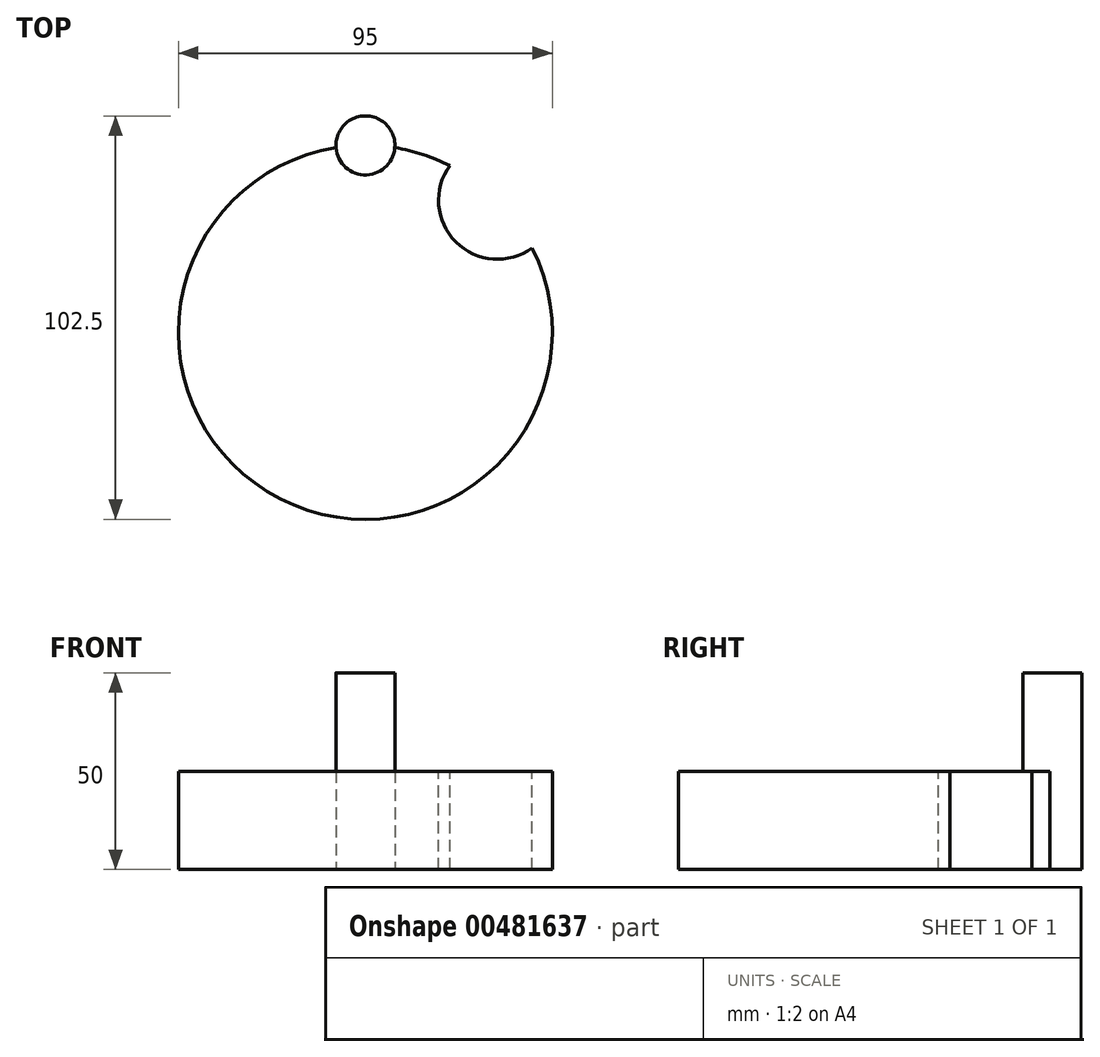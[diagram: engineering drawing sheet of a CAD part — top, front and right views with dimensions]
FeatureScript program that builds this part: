
annotation { "Feature Type Name" : "Feature", "Feature Type Description" : "" }
export const myFeature = defineFeature(function(context is Context, id is Id, definition is map)
    precondition{}
    {
        {
            var Q0;
            Q0=qCreatedBy(makeId("Top.planeOp"),FACE);
            var sketch = newSketch(context, id + "F0", { "sketchPlane" : qUnion([Q0])});
            skCircle(sketch, "E0", {"center": v(0, 0) * mm, "radius": 47.5 * mm});
            skCircle(sketch, "E1", {"center": v(0, 47.5) * mm, "radius": 7.5 * mm});
            skSolve(sketch);
        }
        {
            var Q0;
            {var subQ0=sQuery(id+"F0.wireOp",EDGE,"E1");var subQ1=sQuery(id+"F0.wireOp",EDGE,"E0");var subQ2=makeQuery(id+"F0.imprint","INTERSECT",VERTEX,{"disambiguationData":[OD(0.0)],"derivedFrom":[subQ1,subQ0]});Q0=makeQuery(id+"F0.imprint","IMPRINT",FACE,{"disambiguationData":[TD([[makeQuery(id+"F0.imprint","IMPRINT",EDGE,{"disambiguationData":[TD([[subQ2,-1.0]])],"derivedFrom":subQ1}),1.0]])]});}
            extrude(context, id + "F1", {"entities" : qUnion([Q0]), "depth" : 25 * mm, "offsetDistance" : 25 * mm});
        }
        {
            var Q0;
            {var subQ0=sQuery(id+"F0.wireOp",EDGE,"E1");var subQ1=sQuery(id+"F0.wireOp",EDGE,"E0");var subQ2=makeQuery(id+"F0.imprint","INTERSECT",VERTEX,{"disambiguationData":[OD(0.0)],"derivedFrom":[subQ1,subQ0]});Q0=makeQuery(id+"F0.imprint","IMPRINT",FACE,{"disambiguationData":[TD([[makeQuery(id+"F0.imprint","IMPRINT",EDGE,{"disambiguationData":[TD([[subQ2,1.0]])],"derivedFrom":subQ1}),1.0]])]});}
            var Q1;
            {var subQ0=sQuery(id+"F0.wireOp",EDGE,"E1");var subQ1=sQuery(id+"F0.wireOp",EDGE,"E0");var subQ2=makeQuery(id+"F0.imprint","INTERSECT",VERTEX,{"disambiguationData":[OD(0.0)],"derivedFrom":[subQ1,subQ0]});Q1=makeQuery(id+"F0.imprint","IMPRINT",FACE,{"disambiguationData":[TD([[makeQuery(id+"F0.imprint","IMPRINT",EDGE,{"disambiguationData":[TD([[subQ2,1.0]])],"derivedFrom":subQ1}),-1.0]])]});}
            extrude(context, id + "F2", {"entities" : qUnion([Q0, Q1]), "operationType" : NewBodyOperationType.ADD, "depth" : 50 * mm, "offsetDistance" : 25 * mm});
        }
        {
            var Q0;
            Q0=makeQuery(id+"F1.opExtrude","CAP_FACE",FACE,{"disambiguationData":[OSD([sQuery(id+"F0.wireOp",EDGE,"E0"),sQuery(id+"F0.wireOp",EDGE,"E1")])],"isStart":false});
            var sketch = newSketch(context, id + "F3", { "sketchPlane" : qUnion([Q0])});
            skCircle(sketch, "E2", {"center": v(33.59, 33.59) * mm, "radius": 15 * mm});
            skSolve(sketch);
        }
        {
            var Q0;
            {var subQ0=sQuery(id+"F3.wireOp",EDGE,"E2");var subQ1=sQuery(id+"F0.wireOp",EDGE,"E0");var subQ3=sQuery(id+"F0.wireOp",EDGE,"E1");var subQ5=makeQuery(id+"F2.opExtrude","SWEPT_FACE",FACE,{"disambiguationData":[OSD([subQ3])]});var subQ6=makeQuery(id+"FTU9S2BqntfehKC_1.3.F2.boolean.opBoolean","SPLIT",EDGE,{"disambiguationData":[TD([subQ5])],"derivedFrom":makeQuery(id+"FTU9S2BqntfehKC_1.2.F2.boolean.opBoolean","SPLIT",EDGE,{"disambiguationData":[TD([subQ5])],"derivedFrom":makeQuery(id+"FTU9S2BqntfehKC_1.1.F2.boolean.opBoolean","SPLIT",EDGE,{"disambiguationData":[OD(1.0)],"derivedFrom":makeQuery(id+"F1.opExtrude","CAP_EDGE",EDGE,{"disambiguationData":[OSD([subQ1])],"isStart":false})})})});var subQ7=makeQuery(id+"F3.imprint","INTERSECT",VERTEX,{"disambiguationData":[OD(0.0)],"derivedFrom":[subQ6,subQ0]});Q0=makeQuery(id+"F3.imprint","IMPRINT",FACE,{"disambiguationData":[TD([[makeQuery(id+"F3.imprint","IMPRINT",EDGE,{"disambiguationData":[TD([[subQ7,1.0]])],"derivedFrom":subQ0}),1.0]])]});}
            var Q1;
            {var subQ0=sQuery(id+"F3.wireOp",EDGE,"E2");var subQ1=sQuery(id+"F0.wireOp",EDGE,"E0");var subQ3=sQuery(id+"F0.wireOp",EDGE,"E1");var subQ5=makeQuery(id+"F2.opExtrude","SWEPT_FACE",FACE,{"disambiguationData":[OSD([subQ3])]});var subQ6=makeQuery(id+"FTU9S2BqntfehKC_1.3.F2.boolean.opBoolean","SPLIT",EDGE,{"disambiguationData":[TD([subQ5])],"derivedFrom":makeQuery(id+"FTU9S2BqntfehKC_1.2.F2.boolean.opBoolean","SPLIT",EDGE,{"disambiguationData":[TD([subQ5])],"derivedFrom":makeQuery(id+"FTU9S2BqntfehKC_1.1.F2.boolean.opBoolean","SPLIT",EDGE,{"disambiguationData":[OD(1.0)],"derivedFrom":makeQuery(id+"F1.opExtrude","CAP_EDGE",EDGE,{"disambiguationData":[OSD([subQ1])],"isStart":false})})})});var subQ7=makeQuery(id+"F3.imprint","INTERSECT",VERTEX,{"disambiguationData":[OD(0.0)],"derivedFrom":[subQ6,subQ0]});Q1=makeQuery(id+"F3.imprint","IMPRINT",FACE,{"disambiguationData":[TD([[makeQuery(id+"F3.imprint","IMPRINT",EDGE,{"disambiguationData":[TD([[subQ7,-1.0]])],"derivedFrom":subQ0}),1.0]])]});}
            extrude(context, id + "F4", {"entities" : qUnion([Q0, Q1]), "operationType" : NewBodyOperationType.REMOVE, "endBound" : BoundingType.THROUGH_ALL, "oppositeDirection" : true, "depth" : 25 * mm, "offsetDistance" : 25 * mm});
        }
    });
